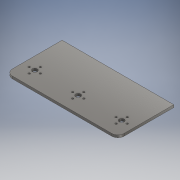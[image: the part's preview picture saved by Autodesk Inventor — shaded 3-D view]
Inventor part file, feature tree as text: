
AUTODESK INVENTOR PART (.ipt)
format: ipt  version: 2018 (Build 220112000, 112)  size: 142,336 bytes
history: native  units: mm
features: other x1, extrude x1, sketch x1
ambient origin geometry x8: Origin, YZ Plane, XZ Plane, XY Plane, X Axis, Y Axis, Z Axis, Center Point
bodies: Body1 (feature_tree)
feature tree (3):
  other  "Sólido1"
  extrude  "Extrusión1"  Depth=45.0mm
  sketch  "Boceto1"  dims[d0=90.0mm d1=45.0mm d4=4.0mm d6=1.5mm d9=1.5mm d10=1.5mm d14=4.0mm d20=1.5mm d21=1.5mm d22=1.5mm d24=1.5mm d25=13.0mm d27=4.0mm d30=4.5mm d34=1.5mm d35=1.5mm d36=1.5mm d38=1.5mm d40=5.0mm d41=2.0mm d42=0.0mm]
